# Revit family: Faucet-Two_Handle-American_Standard-Heritage-7295.152
name_source: partatom
category: Plumbing Fixtures
units: mm (PartAtom-declared; Revit-internal decimal feet)

## family parameters
Cut with Voids When Loaded = No
Host = Face
OmniClass Number = 23.45.55.17
OmniClass Title = Mixing Faucets
Part Type = Normal
Room Calculation Point = No
Round Connector Dimension = Use Diameter
Shared = Yes

## types (1)
- 7295.152.002
    ADA Compliant = Yes
    Assembly Code = D2020300
    CW Connection = Yes
    CWFU = 1.5
    Cold Water Connection Diameter = 1/2"
    Default Elevation = 0"
    Description = Every American Standard Commercial Faucets is designed to work flawlessly and dependably year after year, saving time, money and maintenance headaches.
    Finish = Metal-American_Standard-Brass-002-Polished_Chrome
    Finish -  Handle = Ceramic-American_Standard-Porcelain
    Flow Rate = 2.2 gpm/8.3 L/min
    HW Connection = Yes
    HWFU = 1.5
    Height = 3 7/16"
    Hot Water Connection Diameter = 1/2"
    IAPMO Compliance = ANSI A117.1. ASME A112.18.1, CSA B 125, NSF 61/Section 9 & Annex G
    Installation Type = Wall Mounted
    Length = 14"
    Manufacturer = American Standard
    Material = Metal-American_Standard-Brass-002-Polished_Chrome
    Model = 7295.152.002
    Price = Prices may vary. Please consult Manufacturer Representative for most up-to-date price list.
    Product Documentation Link = https://americanstandard.box.com
    Product Page URL = https://www.americanstandard-us.com
    Revised Date = 03/30/2022
    URL = https://www.americanstandard-us.com
    Vent Connection = No
    WFU = 2
    Warranty Information URL = https://www.americanstandard-us.com
    Waste Connection = No
    Width = 8 3/8"

## geometry (parser evidence)
native form markers: Sweep x2
no freeform markers — native parametric forms only
